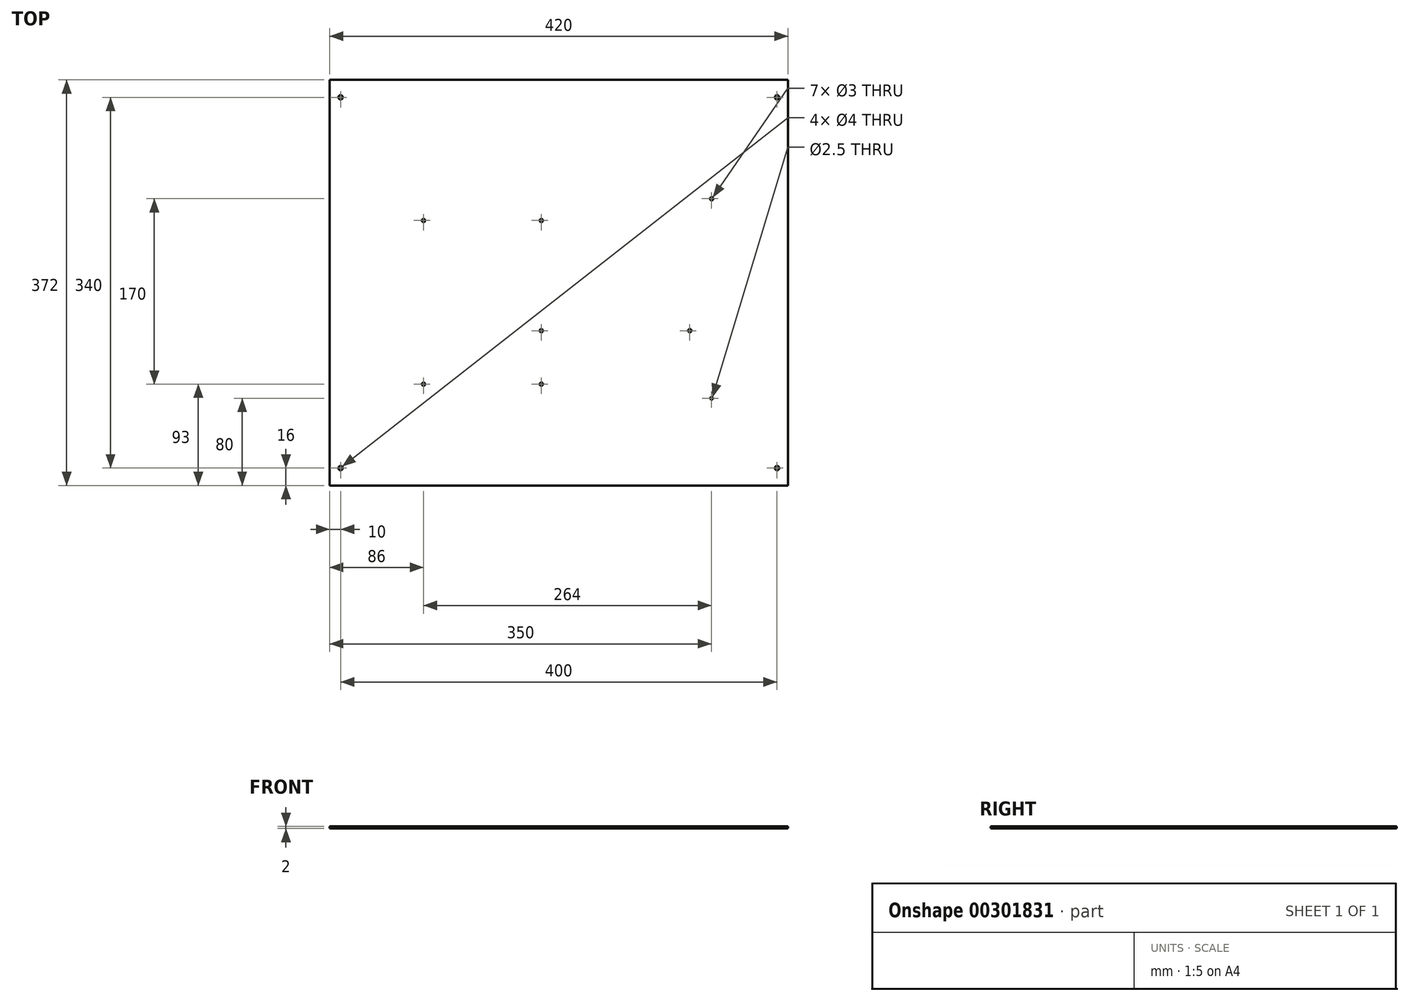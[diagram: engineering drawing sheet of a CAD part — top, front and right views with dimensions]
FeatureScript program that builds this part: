
annotation { "Feature Type Name" : "Feature", "Feature Type Description" : "" }
export const myFeature = defineFeature(function(context is Context, id is Id, definition is map)
    precondition{}
    {
        {
            var Q0;
            Q0=qCreatedBy(makeId("Top.planeOp"),FACE);
            var sketch = newSketch(context, id + "F0", { "sketchPlane" : qUnion([Q0])});
            skLineSegment(sketch, "E0.top", {"start": v(-210, -186) * mm, "end": v(210, -186) * mm});
            skLineSegment(sketch, "E0.left", {"start": v(-210, 186) * mm, "end": v(-210, -186) * mm});
            skLineSegment(sketch, "E0.right", {"start": v(210, 186) * mm, "end": v(210, -186) * mm});
            skPoint(sketch, "E0.middle", {"position": v(0, 0) * mm});
            skCircle(sketch, "E1", {"center": v(-200, -170) * mm, "radius": 2 * mm});
            skCircle(sketch, "E2.MirrorC", {"center": v(-200, 170) * mm, "radius": 2 * mm});
            skCircle(sketch, "E3.MirrorC", {"center": v(200, 170) * mm, "radius": 2 * mm});
            skCircle(sketch, "E4.MirrorC", {"center": v(200, -170) * mm, "radius": 2 * mm});
            skCircle(sketch, "E5", {"center": v(-124, -93) * mm, "radius": 1.5 * mm});
            skCircle(sketch, "E6", {"center": v(140, -106) * mm, "radius": 1.25 * mm});
            skCircle(sketch, "E7", {"center": v(-16, -93) * mm, "radius": 1.5 * mm});
            skCircle(sketch, "E8", {"center": v(-16, -44) * mm, "radius": 1.5 * mm});
            skCircle(sketch, "E9", {"center": v(140, 77) * mm, "radius": 1.5 * mm});
            skCircle(sketch, "E10", {"center": v(120, -44) * mm, "radius": 1.5 * mm});
            skCircle(sketch, "E11", {"center": v(-16, 57) * mm, "radius": 1.5 * mm});
            skLineSegment(sketch, "E12", {"start": v(-210, 186) * mm, "end": v(210, 186) * mm});
            skCircle(sketch, "E13", {"center": v(-124, 57) * mm, "radius": 1.5 * mm});
            skSolve(sketch);
        }
        {
            var Q0;
            Q0 = qSketchRegion(id + "F0", true);
            extrude(context, id + "F1", {"entities" : qUnion([Q0]), "depth" : 2 * mm});
        }
    });
